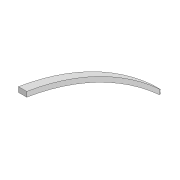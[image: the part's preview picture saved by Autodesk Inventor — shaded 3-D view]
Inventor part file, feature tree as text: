
AUTODESK INVENTOR PART (.ipt)
format: ipt  version: 2022 (Build 260153000, 153)  size: 124,928 bytes
history: native  units: mm
features: extrude x3, sketch x3, projected_geometry x2, fillet x1
ambient origin geometry x8: Origin, YZ Plane, XZ Plane, XY Plane, X Axis, Y Axis, Z Axis, Center Point
bodies: Solid1 (feature_tree)
feature tree (9):
  extrude  "Extrusion1"  Depth=10.0mm
  extrude  "Extrusion2"  Depth=30.0mm
  fillet  "Fillet1"  Radius=120.0mm
  extrude  "Extrusion3"  Depth=2.0mm TaperAngle=0.0deg
  sketch  "Sketch1"  dims[d0=160.0mm d1=10.0mm]
  sketch  "Sketch2"  dims[d2=3.3mm d3=30.0mm d5=120.0mm]
  projected_geometry  "Projected Loop1"
  projected_geometry  "Projected Loop2"
  sketch  "Sketch3"  dims[d6=3.3mm d7=6.0mm d8=0.0mm d9=6.0mm d10=373.775mm d11=90.0mm d12=10.0mm d13=0.0mm d14=2.0mm d15=100.0mm d16=0.0mm]
